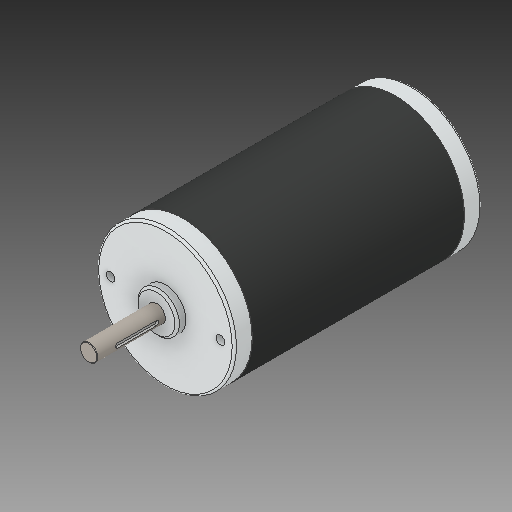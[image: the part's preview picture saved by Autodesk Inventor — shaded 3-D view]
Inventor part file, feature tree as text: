
AUTODESK INVENTOR PART (.ipt)
format: ipt  version: 2017 SP1 (Build 210196100, 196)  size: 165,888 bytes
history: native  units: in
note: dims shown in document units (in); Inventor stores cm internally (conversion verified against a paired STEP export)
features: fillet x1
ambient origin geometry x8: Origin, YZ Plane, XZ Plane, XY Plane, X Axis, Y Axis, Z Axis, Center Point
bodies: Solid1 (feature_tree)
feature tree (1):
  fillet  "Fillet5"  [1 undecoded]
note: 1 required parameter value undecoded (feature->parameter linkage not recoverable at this tier; creation-order binding heuristic only, values carry confidence <= 0.55)
